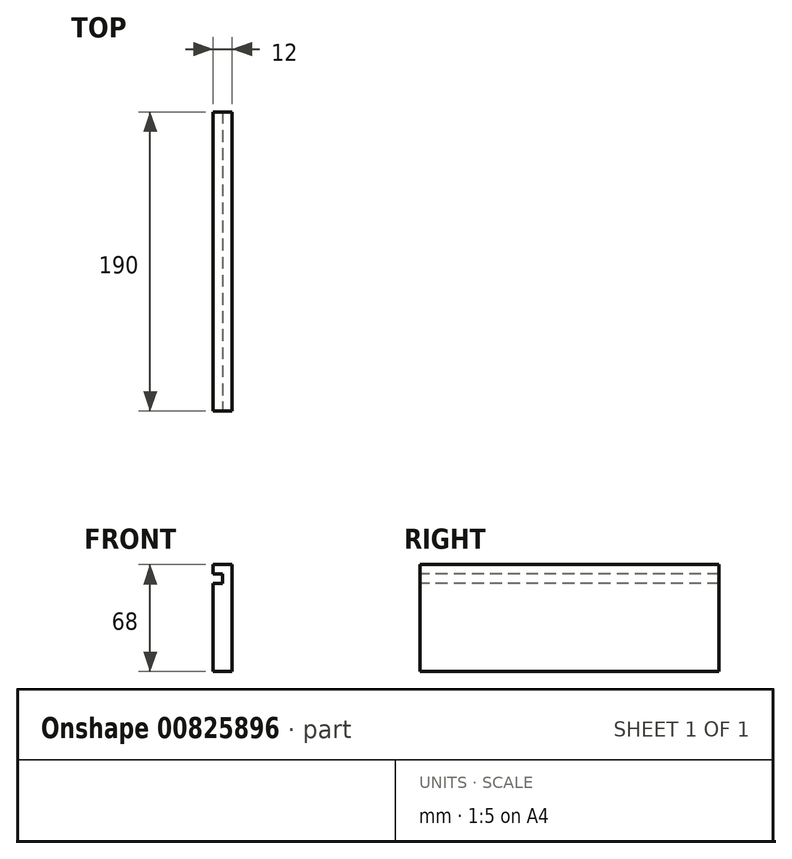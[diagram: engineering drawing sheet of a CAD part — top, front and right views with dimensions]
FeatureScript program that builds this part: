
annotation { "Feature Type Name" : "Feature", "Feature Type Description" : "" }
export const myFeature = defineFeature(function(context is Context, id is Id, definition is map)
    precondition{}
    {
        {
            var Q0;
            Q0=qCreatedBy(makeId("Front.planeOp"),FACE);
            var sketch = newSketch(context, id + "F0", { "sketchPlane" : qUnion([Q0])});
            skLineSegment(sketch, "E0.bottom", {"start": v(0, 0) * mm, "end": v(12, 0) * mm});
            skLineSegment(sketch, "E0.top", {"start": v(0, 68) * mm, "end": v(12, 68) * mm});
            skLineSegment(sketch, "E0.left", {"start": v(0, 0) * mm, "end": v(0, 68) * mm});
            skLineSegment(sketch, "E0.right", {"start": v(12, 0) * mm, "end": v(12, 68) * mm});
            skSolve(sketch);
        }
        {
            var Q0;
            Q0=makeQuery(id+"F0.imprint","IMPRINT",FACE,{"disambiguationData":[TD([[makeQuery(id+"F0.imprint","IMPRINT",EDGE,{"derivedFrom":sQuery(id+"F0.wireOp",EDGE,"E0.bottom")}),1.0]])]});
            extrude(context, id + "F1", {"entities" : qUnion([Q0]), "depth" : 190 * mm, "offsetDistance" : 25 * mm});
        }
        {
            var Q0;
            Q0=makeQuery(id+"F1.opExtrude","CAP_FACE",FACE,{"disambiguationData":[OSD([sQuery(id+"F0.wireOp",EDGE,"E0.bottom"),sQuery(id+"F0.wireOp",EDGE,"E0.top"),sQuery(id+"F0.wireOp",EDGE,"E0.left"),sQuery(id+"F0.wireOp",EDGE,"E0.right")])],"isStart":false});
            var sketch = newSketch(context, id + "F2", { "sketchPlane" : qUnion([Q0])});
            skLineSegment(sketch, "E1", {"start": v(0, 62) * mm, "end": v(6, 62) * mm});
            skLineSegment(sketch, "E2", {"start": v(6, 62) * mm, "end": v(6, 56) * mm});
            skLineSegment(sketch, "E3", {"start": v(6, 56) * mm, "end": v(0, 56) * mm});
            skSolve(sketch);
        }
        {
            var Q0;
            {var subQ0=sQuery(id+"F2.wireOp",EDGE,"E1");Q0=makeQuery(id+"F2.imprint","IMPRINT",FACE,{"disambiguationData":[TD([[makeQuery(id+"F2.imprint","IMPRINT",EDGE,{"derivedFrom":subQ0}),-1.0]])]});}
            extrude(context, id + "F3", {"entities" : qUnion([Q0]), "operationType" : NewBodyOperationType.REMOVE, "oppositeDirection" : true, "depth" : 190 * mm, "offsetDistance" : 25 * mm});
        }
    });
